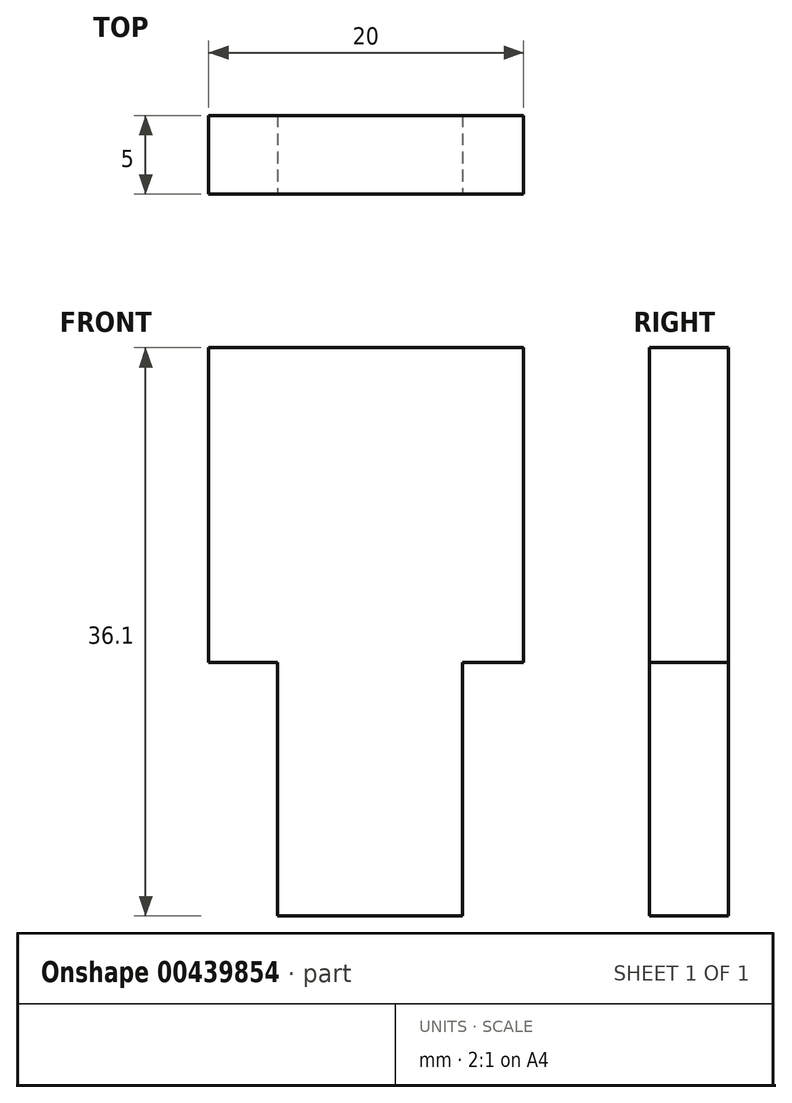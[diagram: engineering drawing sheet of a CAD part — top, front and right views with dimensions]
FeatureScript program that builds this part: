
annotation { "Feature Type Name" : "Feature", "Feature Type Description" : "" }
export const myFeature = defineFeature(function(context is Context, id is Id, definition is map)
    precondition{}
    {
        {
            var Q0;
            Q0=qCreatedBy(makeId("Top.planeOp"),FACE);
            var sketch = newSketch(context, id + "F0", { "sketchPlane" : qUnion([Q0])});
            skLineSegment(sketch, "E0.bottom", {"start": v(-68.55, 6) * mm, "end": v(-48.55, 6) * mm});
            skLineSegment(sketch, "E0.top", {"start": v(-68.55, 1) * mm, "end": v(-48.55, 1) * mm});
            skLineSegment(sketch, "E0.left", {"start": v(-68.55, 6) * mm, "end": v(-68.55, 1) * mm});
            skLineSegment(sketch, "E0.right", {"start": v(-48.55, 6) * mm, "end": v(-48.55, 1) * mm});
            skSolve(sketch);
        }
        {
            var Q0;
            Q0=makeQuery(id+"F0.imprint","IMPRINT",FACE,{"disambiguationData":[TD([[makeQuery(id+"F0.imprint","IMPRINT",EDGE,{"derivedFrom":sQuery(id+"F0.wireOp",EDGE,"E0.bottom")}),-1.0]])]});
            extrude(context, id + "F1", {"entities" : qUnion([Q0]), "depth" : 20 * mm});
        }
        {
            var Q0;
            Q0=makeQuery(id+"F1.opExtrude","CAP_FACE",FACE,{"disambiguationData":[OSD([sQuery(id+"F0.wireOp",EDGE,"E0.bottom"),sQuery(id+"F0.wireOp",EDGE,"E0.top"),sQuery(id+"F0.wireOp",EDGE,"E0.left"),sQuery(id+"F0.wireOp",EDGE,"E0.right")])],"isStart":true});
            var sketch = newSketch(context, id + "F2", { "sketchPlane" : qUnion([Q0])});
            skLineSegment(sketch, "E1.bottom", {"start": v(-64.16, -6) * mm, "end": v(-52.42, -6) * mm});
            skLineSegment(sketch, "E1.top", {"start": v(-64.16, -1) * mm, "end": v(-52.42, -1) * mm});
            skLineSegment(sketch, "E1.left", {"start": v(-64.16, -6) * mm, "end": v(-64.16, -1) * mm});
            skLineSegment(sketch, "E1.right", {"start": v(-52.42, -6) * mm, "end": v(-52.42, -1) * mm});
            skSolve(sketch);
        }
        {
            var Q0;
            Q0 = qSketchRegion(id + "F2", true);
            extrude(context, id + "F3", {"entities" : qUnion([Q0]), "operationType" : NewBodyOperationType.ADD, "depth" : 16.1 * mm});
        }
    });
